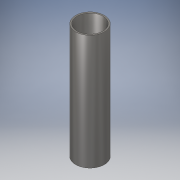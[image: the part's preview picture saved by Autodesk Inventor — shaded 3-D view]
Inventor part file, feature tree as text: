
AUTODESK INVENTOR PART (.ipt)
format: ipt  version: 2018 (Build 220112000, 112)  size: 102,400 bytes
history: native  units: in
note: dims shown in document units (in); Inventor stores cm internally (conversion verified against a paired STEP export)
features: extrude x1, sketch x1
ambient origin geometry x8: Origin, YZ Plane, XZ Plane, XY Plane, X Axis, Y Axis, Z Axis, Center Point
bodies: Solid1 (feature_tree)
feature tree (2):
  extrude  "Extrusion1"  Depth=2.0in
  sketch  "Sketch1"  dims[d0=0.5in d1=0.025in d2=2.0in d3=0.0in]
